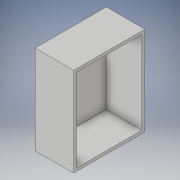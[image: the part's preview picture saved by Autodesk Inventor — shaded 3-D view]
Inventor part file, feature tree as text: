
AUTODESK INVENTOR PART (.ipt)
format: ipt  version: 2018 (Build 220112000, 112)  size: 136,192 bytes
history: native  units: in
note: dims shown in document units (in); Inventor stores cm internally (conversion verified against a paired STEP export)
features: extrude x3, sketch x2
ambient origin geometry x8: Origin, YZ Plane, XZ Plane, XY Plane, X Axis, Y Axis, Z Axis, Center Point
bodies: Solid1 (feature_tree)
feature tree (5):
  sketch  "Sketch1"  dims[d0=30.0in d1=24.0in]
  extrude  "Extrusion3"  Depth=24.0in
  extrude  "Extrusion4"  Depth=12.0in TaperAngle=0.0deg
  extrude  "Extrusion6"  Depth=1.0in TaperAngle=0.0deg
  sketch  "Sketch4"  dims[d2=1.0in d11=12.0in d12=0.0in d13=1.0in d14=0.0in d16=7.0in d17=7.0in d35=2.0in d36=1.1681in d37=2.0in d38=1.1681in d39=2.0in d40=1.1681in d44=36.0in d45=0.0in d46=4.0in d48=0.2031in d50=0.2031in d52=0.2031in d53=9.0in d54=0.9963in d55=9.0in d56=0.9963in]
